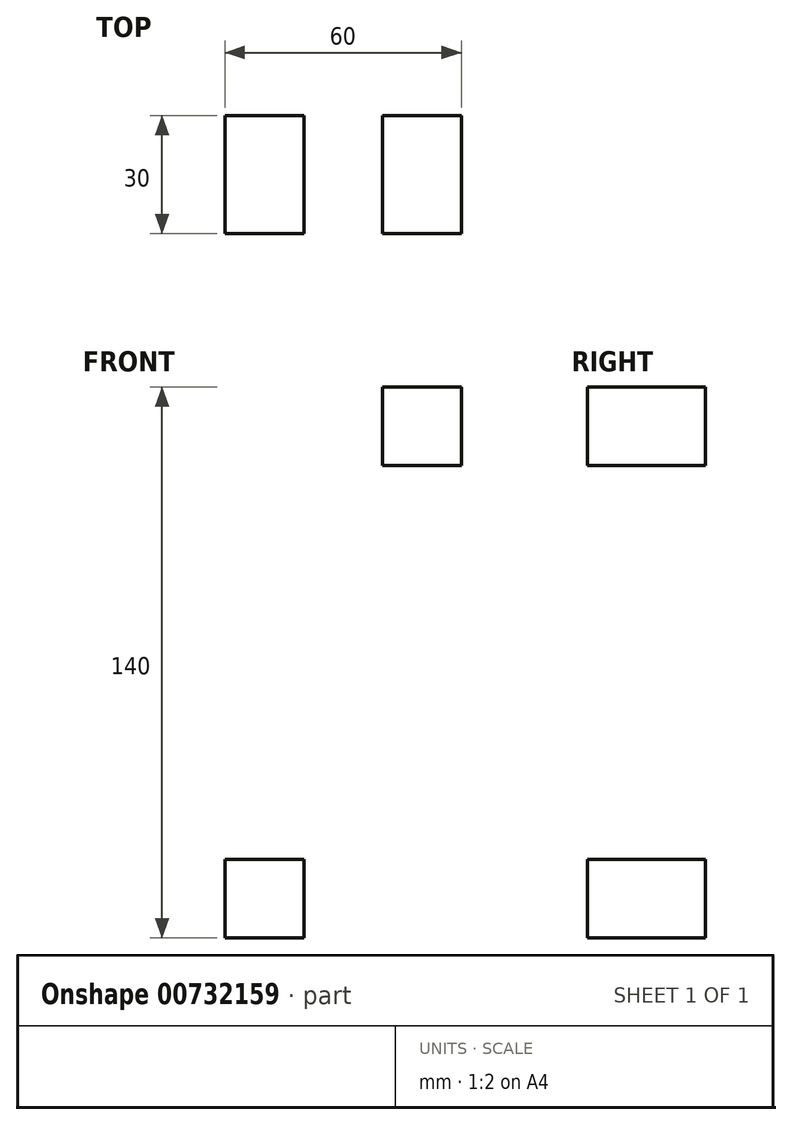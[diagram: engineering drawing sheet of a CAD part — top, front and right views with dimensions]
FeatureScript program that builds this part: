
annotation { "Feature Type Name" : "Feature", "Feature Type Description" : "" }
export const myFeature = defineFeature(function(context is Context, id is Id, definition is map)
    precondition{}
    {
        {
            var Q0;
            Q0=qCreatedBy(makeId("Front.planeOp"),FACE);
            var sketch = newSketch(context, id + "F0", { "sketchPlane" : qUnion([Q0])});
            skLineSegment(sketch, "E0.bottom", {"start": v(0, 0) * mm, "end": v(60, 0) * mm});
            skLineSegment(sketch, "E0.top", {"start": v(0, 140) * mm, "end": v(60, 140) * mm});
            skLineSegment(sketch, "E0.left", {"start": v(0, 0) * mm, "end": v(0, 140) * mm});
            skLineSegment(sketch, "E0.right", {"start": v(60, 0) * mm, "end": v(60, 140) * mm});
            skLineSegment(sketch, "E1.left", {"start": v(20, 30) * mm, "end": v(20, 55) * mm});
            skLineSegment(sketch, "E1.right", {"start": v(40, 30) * mm, "end": v(40, 55) * mm});
            skLineSegment(sketch, "E2.bottom", {"start": v(0, 0) * mm, "end": v(20, 0) * mm});
            skLineSegment(sketch, "E2.top", {"start": v(0, 20) * mm, "end": v(20, 20) * mm});
            skLineSegment(sketch, "E2.left", {"start": v(0, 0) * mm, "end": v(0, 20) * mm});
            skLineSegment(sketch, "E2.right", {"start": v(20, 0) * mm, "end": v(20, 20) * mm});
            skLineSegment(sketch, "E3.bottom", {"start": v(40, 120) * mm, "end": v(60, 120) * mm});
            skLineSegment(sketch, "E3.top", {"start": v(40, 140) * mm, "end": v(60, 140) * mm});
            skLineSegment(sketch, "E3.left", {"start": v(40, 120) * mm, "end": v(40, 140) * mm});
            skLineSegment(sketch, "E3.right", {"start": v(60, 120) * mm, "end": v(60, 140) * mm});
            skArc(sketch, "E4", {"start": v(40, 110) * mm, "mid": v(30, 120) * mm, "end": v(20, 110) * mm});
            skPoint(sketch, "E4.first.point", {"position": v(20, 110) * mm});
            skPoint(sketch, "E4.second.point", {"position": v(40, 110) * mm});
            skPoint(sketch, "E4.third.point", {"position": v(30, 120) * mm});
            skArc(sketch, "E5", {"start": v(20, 30) * mm, "mid": v(30, 20) * mm, "end": v(40, 30) * mm});
            skPoint(sketch, "E5.first.point", {"position": v(20, 30) * mm});
            skPoint(sketch, "E5.second.point", {"position": v(40, 30) * mm});
            skPoint(sketch, "E5.third.point", {"position": v(30, 20) * mm});
            skLineSegment(sketch, "E6", {"start": v(20, 110) * mm, "end": v(20, 85) * mm});
            skArc(sketch, "E7", {"start": v(40, 55) * mm, "mid": v(30, 65) * mm, "end": v(20, 55) * mm});
            skPoint(sketch, "E7.second.point", {"position": v(40, 55) * mm});
            skPoint(sketch, "E7.third.point", {"position": v(33.85, 64.23) * mm});
            skArc(sketch, "E8", {"start": v(20, 85) * mm, "mid": v(30, 75) * mm, "end": v(40, 85) * mm});
            skPoint(sketch, "E8.second.point", {"position": v(40, 85) * mm});
            skPoint(sketch, "E8.third.point", {"position": v(28.18, 75.17) * mm});
            skPoint(sketch, "E9.orphan", {"position": v(20, 120) * mm});
            skLineSegment(sketch, "E10.trimOffspring", {"start": v(20, 85) * mm, "end": v(20, 110) * mm});
            skLineSegment(sketch, "E11.trimOffspring", {"start": v(40, 85) * mm, "end": v(40, 110) * mm});
            skSolve(sketch);
        }
        {
            var Q0;
            Q0=makeQuery(id+"F0.imprint","IMPRINT",FACE,{"disambiguationData":[TD([[makeQuery(id+"F0.imprint","IMPRINT",EDGE,{"derivedFrom":sQuery(id+"F0.wireOp",EDGE,"E0.bottom")}),1.0]])]});
            var Q1;
            Q1=makeQuery(id+"F0.imprint","IMPRINT",FACE,{"disambiguationData":[TD([[makeQuery(id+"F0.imprint","IMPRINT",EDGE,{"derivedFrom":sQuery(id+"F0.wireOp",EDGE,"E3.bottom")}),1.0]])]});
            var Q2;
            Q2=makeQuery(id+"F0.imprint","IMPRINT",FACE,{"disambiguationData":[TD([[makeQuery(id+"F0.imprint","IMPRINT",EDGE,{"derivedFrom":sQuery(id+"F0.wireOp",EDGE,"E2.bottom")}),1.0]])]});
            extrude(context, id + "F1", {"entities" : qUnion([Q0, Q1, Q2]), "depth" : 30 * mm, "offsetDistance" : 25 * mm});
        }
    });
